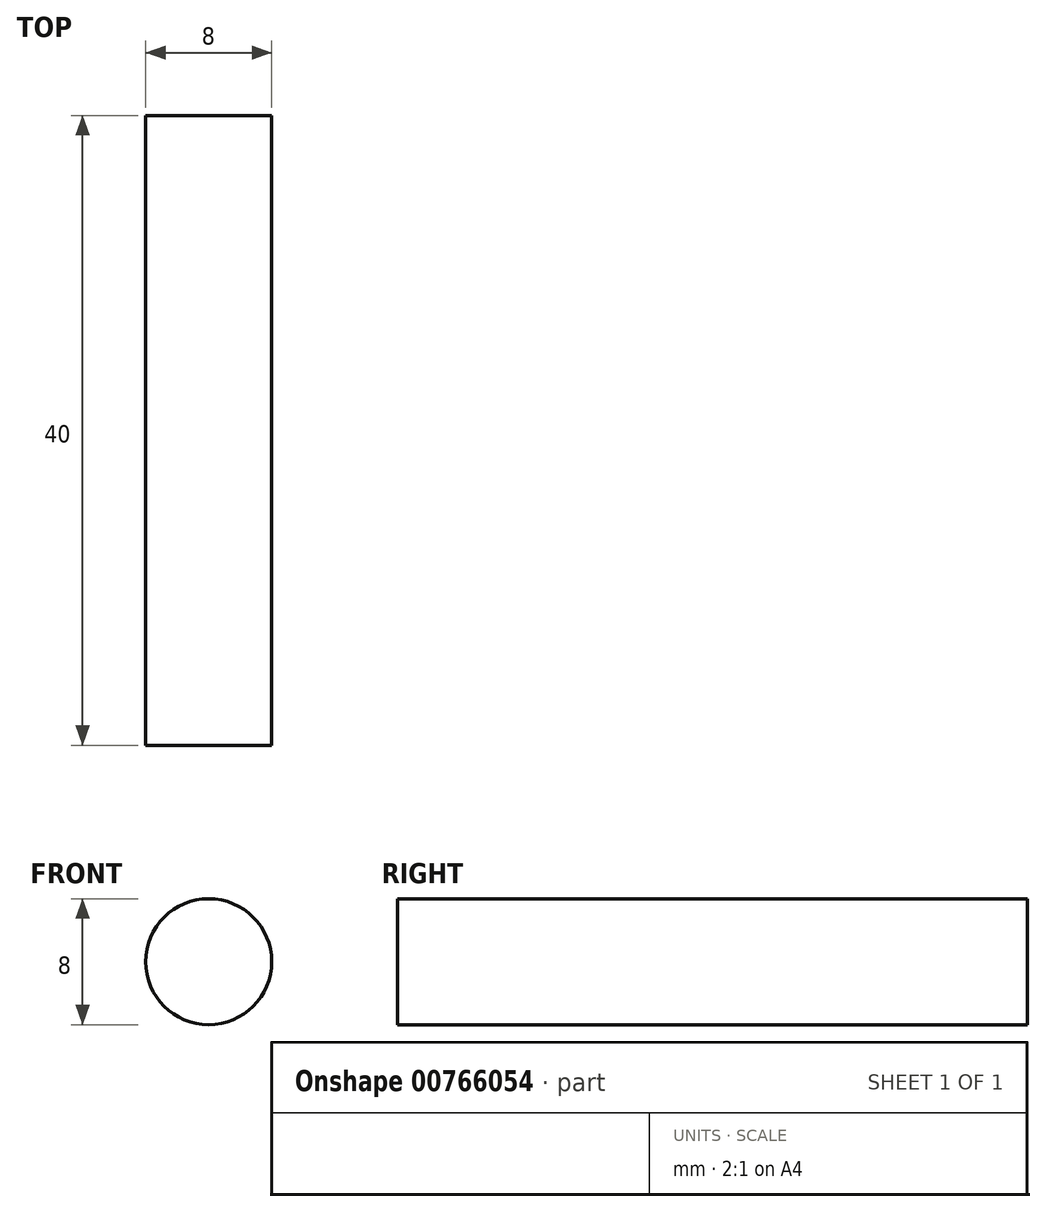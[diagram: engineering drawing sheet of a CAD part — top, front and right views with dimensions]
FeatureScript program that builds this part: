
annotation { "Feature Type Name" : "Feature", "Feature Type Description" : "" }
export const myFeature = defineFeature(function(context is Context, id is Id, definition is map)
    precondition{}
    {
        {
            var Q0;
            Q0=qCreatedBy(makeId("Front.planeOp"),FACE);
            var sketch = newSketch(context, id + "F0", { "sketchPlane" : qUnion([Q0])});
            skCircle(sketch, "E0", {"center": v(0, 0) * mm, "radius": 4 * mm});
            skSolve(sketch);
        }
        {
            var Q0;
            Q0=makeQuery(id+"F0.imprint","IMPRINT",FACE,{"disambiguationData":[TD([[makeQuery(id+"F0.imprint","IMPRINT",EDGE,{"derivedFrom":sQuery(id+"F0.wireOp",EDGE,"E0")}),1.0]])]});
            extrude(context, id + "F1", {"entities" : qUnion([Q0]), "depth" : 40 * mm, "offsetDistance" : 25 * mm});
        }
    });
